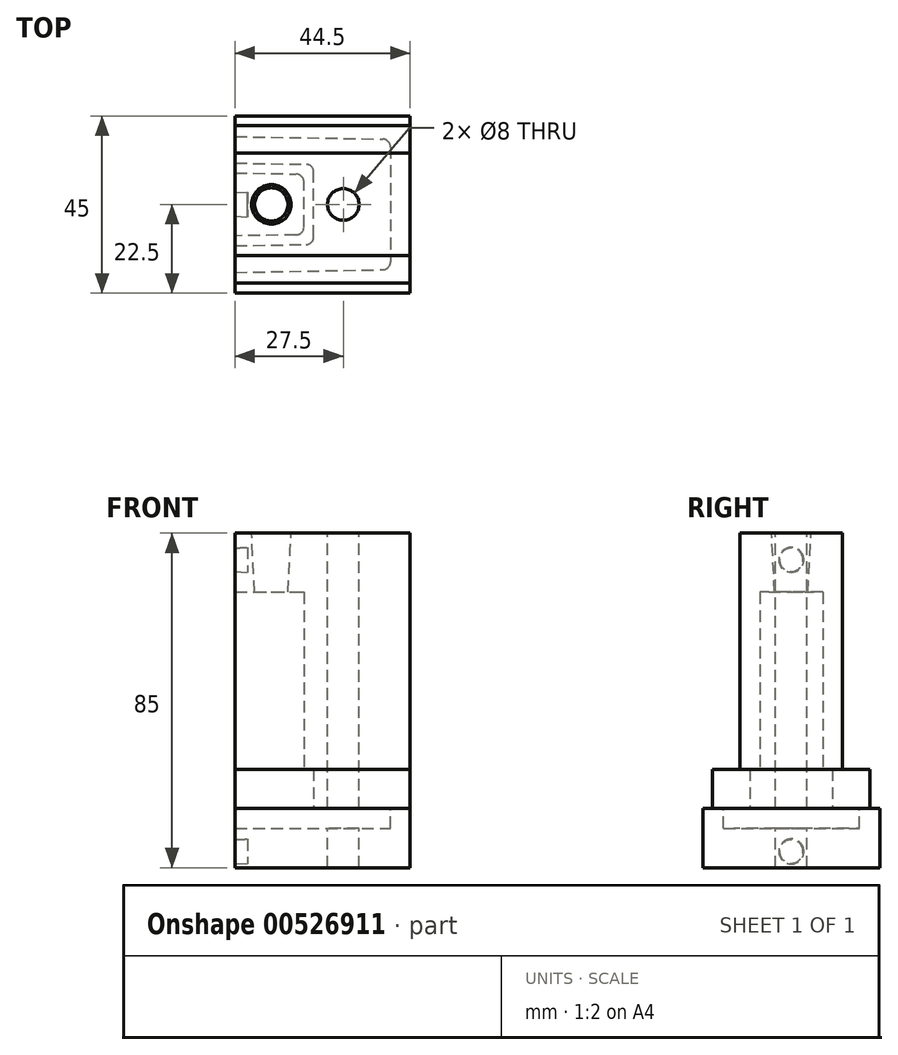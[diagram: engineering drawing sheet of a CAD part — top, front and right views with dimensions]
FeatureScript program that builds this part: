
annotation { "Feature Type Name" : "Feature", "Feature Type Description" : "" }
export const myFeature = defineFeature(function(context is Context, id is Id, definition is map)
    precondition{}
    {
        {
            var Q0;
            Q0=qCreatedBy(makeId("Top.planeOp"),FACE);
            var sketch = newSketch(context, id + "F0", { "sketchPlane" : qUnion([Q0])});
            skLineSegment(sketch, "E0.bottom", {"start": v(44.4, -13) * mm, "end": v(-44.4, -13) * mm});
            skLineSegment(sketch, "E0.top", {"start": v(44.4, 13) * mm, "end": v(-44.4, 13) * mm});
            skLineSegment(sketch, "E0.left", {"start": v(44.4, -13) * mm, "end": v(44.4, 13) * mm});
            skLineSegment(sketch, "E0.right", {"start": v(-44.4, -13) * mm, "end": v(-44.4, 13) * mm});
            skPoint(sketch, "E0.middle", {"position": v(0, 0) * mm});
            skSolve(sketch);
        }
        {
            var Q0;
            Q0=qSketchRegion(id+"F0",true);
            extrude(context, id + "F1", {"entities" : qUnion([Q0]), "depth" : 60 * mm, "offsetDistance" : 25 * mm});
        }
        {
            var Q0;
            Q0=makeQuery(id+"F1.opExtrude","CAP_FACE",FACE,{"disambiguationData":[OSD([sQuery(id+"F0.wireOp",EDGE,"E0.bottom"),sQuery(id+"F0.wireOp",EDGE,"E0.top"),sQuery(id+"F0.wireOp",EDGE,"E0.left"),sQuery(id+"F0.wireOp",EDGE,"E0.right")])],"isStart":true});
            var sketch = newSketch(context, id + "F2", { "sketchPlane" : qUnion([Q0])});
            skPoint(sketch, "E1.middle", {"position": v(0, 0) * mm});
            skLineSegment(sketch, "E2", {"start": v(0, -8) * mm, "end": v(-17.5, -7.7) * mm});
            skLineSegment(sketch, "E3", {"start": v(0, -8) * mm, "end": v(17.5, -7.7) * mm});
            skLineSegment(sketch, "E4", {"start": v(0, 8) * mm, "end": v(-17.5, 7.7) * mm});
            skLineSegment(sketch, "E5", {"start": v(17.5, 7.7) * mm, "end": v(0, 8) * mm});
            skLineSegment(sketch, "E6", {"start": v(-17.5, 7.7) * mm, "end": v(-17.5, -7.7) * mm});
            skLineSegment(sketch, "E7", {"start": v(17.5, 7.7) * mm, "end": v(17.5, -7.7) * mm});
            skSolve(sketch);
        }
        {
            var Q0;
            Q0=qSketchRegion(id+"F2",true);
            extrude(context, id + "F3", {"entities" : qUnion([Q0]), "operationType" : NewBodyOperationType.REMOVE, "oppositeDirection" : true, "depth" : 45 * mm, "offsetDistance" : 25 * mm});
        }
        {
            var Q0;
            Q0=makeQuery(id+"F3.boolean.opBoolean","COPY",EDGE,{"derivedFrom":makeQuery(id+"F3.opExtrude","SWEPT_EDGE",EDGE,{"disambiguationData":[OSD([sQuery(id+"F2.wireOp",EDGE,"E2"),sQuery(id+"F2.wireOp",EDGE,"E6")])]})});
            var Q1;
            Q1=makeQuery(id+"F3.boolean.opBoolean","COPY",EDGE,{"derivedFrom":makeQuery(id+"F3.opExtrude","SWEPT_EDGE",EDGE,{"disambiguationData":[OSD([sQuery(id+"F2.wireOp",EDGE,"E4"),sQuery(id+"F2.wireOp",EDGE,"E6")])]})});
            var Q2;
            Q2=makeQuery(id+"F3.boolean.opBoolean","COPY",EDGE,{"derivedFrom":makeQuery(id+"F3.opExtrude","SWEPT_EDGE",EDGE,{"disambiguationData":[OSD([sQuery(id+"F2.wireOp",EDGE,"E5"),sQuery(id+"F2.wireOp",EDGE,"E7")])]})});
            var Q3;
            Q3=makeQuery(id+"F3.boolean.opBoolean","COPY",EDGE,{"derivedFrom":makeQuery(id+"F3.opExtrude","SWEPT_EDGE",EDGE,{"disambiguationData":[OSD([sQuery(id+"F2.wireOp",EDGE,"E3"),sQuery(id+"F2.wireOp",EDGE,"E7")])]})});
            fillet(context, id + "F4", {"entities" : qUnion([Q0, Q1, Q2, Q3]), "radius" : 2 * mm, "tangentPropagation" : true, "allowEdgeOverflow" : false});
        }
        {
            var Q0;
            Q0=makeQuery(id+"F1.opExtrude","CAP_FACE",FACE,{"disambiguationData":[OSD([sQuery(id+"F0.wireOp",EDGE,"E0.bottom"),sQuery(id+"F0.wireOp",EDGE,"E0.top"),sQuery(id+"F0.wireOp",EDGE,"E0.left"),sQuery(id+"F0.wireOp",EDGE,"E0.right")])],"isStart":true});
            var sketch = newSketch(context, id + "F5", { "sketchPlane" : qUnion([Q0])});
            skLineSegment(sketch, "E8.bottom", {"start": v(44.45, -20) * mm, "end": v(-44.45, -20) * mm});
            skLineSegment(sketch, "E8.top", {"start": v(44.45, 20) * mm, "end": v(-44.45, 20) * mm});
            skLineSegment(sketch, "E8.left", {"start": v(44.45, -20) * mm, "end": v(44.45, 20) * mm});
            skLineSegment(sketch, "E8.right", {"start": v(-44.45, -20) * mm, "end": v(-44.45, 20) * mm});
            skPoint(sketch, "E8.middle", {"position": v(0, 0) * mm});
            skSolve(sketch);
        }
        {
            var Q0;
            Q0=qSketchRegion(id+"F5",true);
            extrude(context, id + "F6", {"entities" : qUnion([Q0]), "operationType" : NewBodyOperationType.ADD, "depth" : 10 * mm, "offsetDistance" : 25 * mm});
        }
        {
            var Q0;
            Q0=makeQuery(id+"F6.opExtrude","CAP_FACE",FACE,{"disambiguationData":[OSD([sQuery(id+"F5.wireOp",EDGE,"E8.bottom"),sQuery(id+"F5.wireOp",EDGE,"E8.top"),sQuery(id+"F5.wireOp",EDGE,"E8.left"),sQuery(id+"F5.wireOp",EDGE,"E8.right")])],"isStart":false});
            var sketch = newSketch(context, id + "F7", { "sketchPlane" : qUnion([Q0])});
            skPoint(sketch, "E9.middle", {"position": v(0, 0) * mm});
            skLineSegment(sketch, "E10", {"start": v(0, -10.5) * mm, "end": v(20, -10.15) * mm});
            skLineSegment(sketch, "E11", {"start": v(0, -10.5) * mm, "end": v(-20, -10.15) * mm});
            skLineSegment(sketch, "E12", {"start": v(-20, 10.15) * mm, "end": v(0, 10.5) * mm});
            skLineSegment(sketch, "E13", {"start": v(0, 10.5) * mm, "end": v(20, 10.15) * mm});
            skLineSegment(sketch, "E14", {"start": v(20, 10.15) * mm, "end": v(20, -10.15) * mm});
            skLineSegment(sketch, "E15", {"start": v(-20, 10.15) * mm, "end": v(-20, -10.15) * mm});
            skSolve(sketch);
        }
        {
            var Q0;
            Q0=qSketchRegion(id+"F7",true);
            extrude(context, id + "F8", {"entities" : qUnion([Q0]), "operationType" : NewBodyOperationType.REMOVE, "oppositeDirection" : true, "depth" : 10 * mm, "offsetDistance" : 25 * mm});
        }
        {
            var Q0;
            Q0=makeQuery(id+"F8.boolean.opBoolean","COPY",EDGE,{"derivedFrom":makeQuery(id+"F8.opExtrude","SWEPT_EDGE",EDGE,{"disambiguationData":[OSD([sQuery(id+"F7.wireOp",EDGE,"E11"),sQuery(id+"F7.wireOp",EDGE,"E15")])]})});
            var Q1;
            Q1=makeQuery(id+"F8.boolean.opBoolean","COPY",EDGE,{"derivedFrom":makeQuery(id+"F8.opExtrude","SWEPT_EDGE",EDGE,{"disambiguationData":[OSD([sQuery(id+"F7.wireOp",EDGE,"E12"),sQuery(id+"F7.wireOp",EDGE,"E15")])]})});
            var Q2;
            Q2=makeQuery(id+"F8.boolean.opBoolean","COPY",EDGE,{"derivedFrom":makeQuery(id+"F8.opExtrude","SWEPT_EDGE",EDGE,{"disambiguationData":[OSD([sQuery(id+"F7.wireOp",EDGE,"E10"),sQuery(id+"F7.wireOp",EDGE,"E14")])]})});
            var Q3;
            Q3=makeQuery(id+"F8.boolean.opBoolean","COPY",EDGE,{"derivedFrom":makeQuery(id+"F8.opExtrude","SWEPT_EDGE",EDGE,{"disambiguationData":[OSD([sQuery(id+"F7.wireOp",EDGE,"E13"),sQuery(id+"F7.wireOp",EDGE,"E14")])]})});
            fillet(context, id + "F9", {"entities" : qUnion([Q0, Q1, Q2, Q3]), "radius" : 2 * mm, "tangentPropagation" : true, "allowEdgeOverflow" : false});
        }
        {
            var Q0;
            Q0=makeQuery(id+"F6.opExtrude","CAP_FACE",FACE,{"disambiguationData":[OSD([sQuery(id+"F5.wireOp",EDGE,"E8.bottom"),sQuery(id+"F5.wireOp",EDGE,"E8.top"),sQuery(id+"F5.wireOp",EDGE,"E8.left"),sQuery(id+"F5.wireOp",EDGE,"E8.right")])],"isStart":false});
            var sketch = newSketch(context, id + "F10", { "sketchPlane" : qUnion([Q0])});
            skLineSegment(sketch, "E16.bottom", {"start": v(44.5, -22.5) * mm, "end": v(-44.5, -22.5) * mm});
            skLineSegment(sketch, "E16.top", {"start": v(44.5, 22.5) * mm, "end": v(-44.5, 22.5) * mm});
            skLineSegment(sketch, "E16.left", {"start": v(44.5, -22.5) * mm, "end": v(44.5, 22.5) * mm});
            skLineSegment(sketch, "E16.right", {"start": v(-44.5, -22.5) * mm, "end": v(-44.5, 22.5) * mm});
            skPoint(sketch, "E16.middle", {"position": v(0, 0) * mm});
            skSolve(sketch);
        }
        {
            var Q0;
            Q0=qSketchRegion(id+"F10",true);
            extrude(context, id + "F11", {"entities" : qUnion([Q0]), "operationType" : NewBodyOperationType.ADD, "depth" : 15 * mm, "offsetDistance" : 25 * mm});
        }
        {
            var Q0;
            {var subQ0=sQuery(id+"F10.wireOp",EDGE,"E16.bottom");var subQ1=sQuery(id+"F10.wireOp",EDGE,"E16.top");var subQ2=sQuery(id+"F10.wireOp",EDGE,"E16.left");var subQ3=sQuery(id+"F10.wireOp",EDGE,"E16.right");Q0=makeQuery(id+"F11.boolean.opBoolean","SPLIT",FACE,{"disambiguationData":[TD([makeQuery(id+"F6.opExtrude","SWEPT_FACE",FACE,{"disambiguationData":[OSD([sQuery(id+"F5.wireOp",EDGE,"E8.bottom")])]})])],"derivedFrom":makeQuery(id+"F11.opExtrude","CAP_FACE",FACE,{"disambiguationData":[OSD([subQ0,subQ1,subQ2,subQ3])],"isStart":true})});}
            var sketch = newSketch(context, id + "F12", { "sketchPlane" : qUnion([Q0])});
            skPoint(sketch, "E17.middle", {"position": v(0, 0) * mm});
            skLineSegment(sketch, "E18", {"start": v(0, -17.25) * mm, "end": v(39.5, -16.56) * mm});
            skLineSegment(sketch, "E19", {"start": v(0, -17.25) * mm, "end": v(-44.45, -17.25) * mm});
            skLineSegment(sketch, "E20", {"start": v(-39.5, -16.56) * mm, "end": v(0, -17.25) * mm});
            skLineSegment(sketch, "E21", {"start": v(0, 17.25) * mm, "end": v(-39.5, 16.56) * mm});
            skLineSegment(sketch, "E22", {"start": v(0, 17.25) * mm, "end": v(39.5, 16.56) * mm});
            skLineSegment(sketch, "E23", {"start": v(-39.5, 16.56) * mm, "end": v(-39.5, -16.56) * mm});
            skLineSegment(sketch, "E24", {"start": v(39.5, 16.56) * mm, "end": v(39.5, -16.56) * mm});
            skSolve(sketch);
        }
        {
            var Q0;
            Q0=qSketchRegion(id+"F12",true);
            extrude(context, id + "F13", {"entities" : qUnion([Q0]), "operationType" : NewBodyOperationType.REMOVE, "oppositeDirection" : true, "depth" : 5 * mm, "offsetDistance" : 25 * mm});
        }
        {
            var Q0;
            Q0=makeQuery(id+"F13.boolean.opBoolean","COPY",EDGE,{"derivedFrom":makeQuery(id+"F13.opExtrude","SWEPT_EDGE",EDGE,{"disambiguationData":[OSD([sQuery(id+"F12.wireOp",EDGE,"E21"),sQuery(id+"F12.wireOp",EDGE,"E23")])]})});
            var Q1;
            Q1=makeQuery(id+"F13.boolean.opBoolean","COPY",EDGE,{"derivedFrom":makeQuery(id+"F13.opExtrude","SWEPT_EDGE",EDGE,{"disambiguationData":[OSD([sQuery(id+"F12.wireOp",EDGE,"E20"),sQuery(id+"F12.wireOp",EDGE,"E23")])]})});
            var Q2;
            Q2=makeQuery(id+"F13.boolean.opBoolean","COPY",EDGE,{"derivedFrom":makeQuery(id+"F13.opExtrude","SWEPT_EDGE",EDGE,{"disambiguationData":[OSD([sQuery(id+"F12.wireOp",EDGE,"E18"),sQuery(id+"F12.wireOp",EDGE,"E24")])]})});
            var Q3;
            Q3=makeQuery(id+"F13.boolean.opBoolean","COPY",EDGE,{"derivedFrom":makeQuery(id+"F13.opExtrude","SWEPT_EDGE",EDGE,{"disambiguationData":[OSD([sQuery(id+"F12.wireOp",EDGE,"E22"),sQuery(id+"F12.wireOp",EDGE,"E24")])]})});
            fillet(context, id + "F14", {"entities" : qUnion([Q0, Q1, Q2, Q3]), "radius" : 2 * mm, "tangentPropagation" : true, "allowEdgeOverflow" : false});
        }
        {
            var Q0;
            Q0=makeQuery(id+"F1.opExtrude","CAP_FACE",FACE,{"disambiguationData":[OSD([sQuery(id+"F0.wireOp",EDGE,"E0.bottom"),sQuery(id+"F0.wireOp",EDGE,"E0.top"),sQuery(id+"F0.wireOp",EDGE,"E0.left"),sQuery(id+"F0.wireOp",EDGE,"E0.right")])],"isStart":false});
            var sketch = newSketch(context, id + "F15", { "sketchPlane" : qUnion([Q0])});
            skCircle(sketch, "E25", {"center": v(27.5, 0) * mm, "radius": 4 * mm});
            skCircle(sketch, "E26", {"center": v(-27.5, 0) * mm, "radius": 4.67 * mm});
            skSolve(sketch);
        }
        {
            var Q0;
            Q0=makeQuery(id+"F15.imprint","IMPRINT",FACE,{"disambiguationData":[TD([[makeQuery(id+"F15.imprint","IMPRINT",EDGE,{"derivedFrom":sQuery(id+"F15.wireOp",EDGE,"E26")}),1.0]])]});
            var Q1;
            Q1=makeQuery(id+"F15.imprint","IMPRINT",FACE,{"disambiguationData":[TD([[makeQuery(id+"F15.imprint","IMPRINT",EDGE,{"derivedFrom":sQuery(id+"F15.wireOp",EDGE,"E25")}),1.0]])]});
            var Q2;
            Q2=sQuery(id+"F15.wireOp",EDGE,"E26");
            var Q3;
            Q3=sQuery(id+"F15.wireOp",EDGE,"E25");
            extrude(context, id + "F16", {"entities" : qUnion([Q0, Q1]), "operationType" : NewBodyOperationType.REMOVE, "surfaceEntities" : qUnion([Q2, Q3]), "endBound" : BoundingType.THROUGH_ALL, "oppositeDirection" : true, "depth" : 90 * mm, "offsetDistance" : 25 * mm});
        }
        {
            var Q0;
            Q0=qCreatedBy(makeId("Right.planeOp"),FACE);
            var sketch = newSketch(context, id + "F17", { "sketchPlane" : qUnion([Q0])});
            skLineSegment(sketch, "E27.bottom", {"start": v(-35.8, 69.27) * mm, "end": v(43.73, 69.27) * mm});
            skLineSegment(sketch, "E27.top", {"start": v(-35.8, -49.53) * mm, "end": v(43.73, -49.53) * mm});
            skLineSegment(sketch, "E27.left", {"start": v(-35.8, 69.27) * mm, "end": v(-35.8, -49.53) * mm});
            skLineSegment(sketch, "E27.right", {"start": v(43.73, 69.27) * mm, "end": v(43.73, -49.53) * mm});
            skSolve(sketch);
        }
        {
            var Q0;
            Q0=qSketchRegion(id+"F17",true);
            extrude(context, id + "F18", {"entities" : qUnion([Q0]), "operationType" : NewBodyOperationType.REMOVE, "oppositeDirection" : true, "depth" : 80 * mm, "offsetDistance" : 25 * mm});
        }
        {
            var Q0;
            Q0=makeQuery(id+"F18.boolean.opBoolean","COPY",FACE,{"derivedFrom":makeQuery(id+"F18.opExtrude","CAP_FACE",FACE,{"disambiguationData":[OSD([sQuery(id+"F17.wireOp",EDGE,"E27.bottom"),sQuery(id+"F17.wireOp",EDGE,"E27.top"),sQuery(id+"F17.wireOp",EDGE,"E27.left"),sQuery(id+"F17.wireOp",EDGE,"E27.right")])],"isStart":true})});
            var sketch = newSketch(context, id + "F19", { "sketchPlane" : qUnion([Q0])});
            skCircle(sketch, "E28", {"center": v(0, 53.2) * mm, "radius": 3 * mm});
            skCircle(sketch, "E29", {"center": v(0, -20.9) * mm, "radius": 3 * mm});
            skSolve(sketch);
        }
        {
            var Q0;
            Q0=qSketchRegion(id+"F19",true);
            extrude(context, id + "F20", {"entities" : qUnion([Q0]), "operationType" : NewBodyOperationType.REMOVE, "oppositeDirection" : true, "depth" : 3.2 * mm, "offsetDistance" : 25 * mm, "hasDraft" : true, "draftAngle" : 3 * degree});
        }
        {
            var Q0;
            Q0=makeQuery(id+"F3.boolean.opBoolean","COPY",FACE,{"derivedFrom":makeQuery(id+"F3.opExtrude","CAP_FACE",FACE,{"disambiguationData":[OSD([sQuery(id+"F2.wireOp",EDGE,"E2"),sQuery(id+"F2.wireOp",EDGE,"E3"),sQuery(id+"F2.wireOp",EDGE,"E4"),sQuery(id+"F2.wireOp",EDGE,"E5"),sQuery(id+"F2.wireOp",EDGE,"E6"),sQuery(id+"F2.wireOp",EDGE,"E7")])],"isStart":false})});
            var sketch = newSketch(context, id + "F21", { "sketchPlane" : qUnion([Q0])});
            skCircle(sketch, "E30", {"center": v(9.22, 0) * mm, "radius": 4.23 * mm});
            skSolve(sketch);
        }
        {
            var Q0;
            Q0 = qSketchRegion(id + "F21", true);
            extrude(context, id + "F22", {"entities" : qUnion([Q0]), "operationType" : NewBodyOperationType.REMOVE, "oppositeDirection" : true, "depth" : 25 * mm, "offsetDistance" : 25 * mm, "hasDraft" : true, "draftAngle" : 3 * degree});
        }
    });
